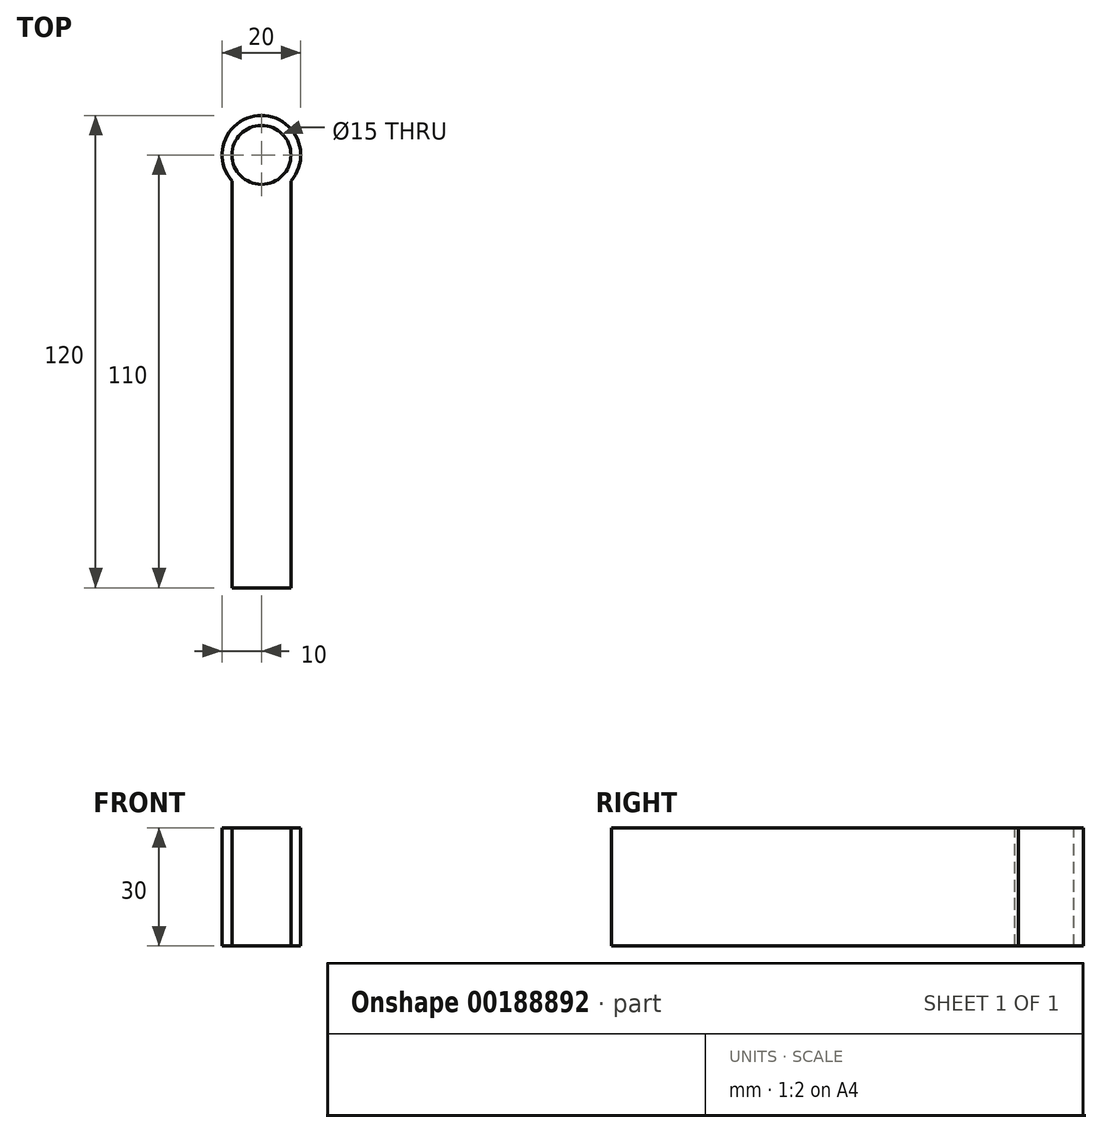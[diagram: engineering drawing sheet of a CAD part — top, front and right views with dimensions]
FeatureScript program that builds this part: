
annotation { "Feature Type Name" : "Feature", "Feature Type Description" : "" }
export const myFeature = defineFeature(function(context is Context, id is Id, definition is map)
    precondition{}
    {
        {
            var Q0;
            Q0=qCreatedBy(makeId("Top.planeOp"),FACE);
            var sketch = newSketch(context, id + "F0", { "sketchPlane" : qUnion([Q0])});
            skCircle(sketch, "E0", {"center": v(0, 0) * mm, "radius": 10 * mm});
            skSolve(sketch);
        }
        {
            var Q0;
            Q0=qSketchRegion(id+"F0",true);
            extrude(context, id + "F1", {"entities" : qUnion([Q0]), "depth" : 30 * mm});
        }
        {
            var Q0;
            Q0=qCreatedBy(makeId("Front.planeOp"),FACE);
            var sketch = newSketch(context, id + "F2", { "sketchPlane" : qUnion([Q0])});
            skLineSegment(sketch, "E1.bottom", {"start": v(-7.5, 30) * mm, "end": v(7.5, 30) * mm});
            skLineSegment(sketch, "E1.top", {"start": v(-7.5, 0) * mm, "end": v(7.5, 0) * mm});
            skLineSegment(sketch, "E1.left", {"start": v(-7.5, 30) * mm, "end": v(-7.5, 0) * mm});
            skLineSegment(sketch, "E1.right", {"start": v(7.5, 30) * mm, "end": v(7.5, 0) * mm});
            skSolve(sketch);
        }
        {
            var Q0;
            Q0=qSketchRegion(id+"F2",true);
            extrude(context, id + "F3", {"entities" : qUnion([Q0]), "operationType" : NewBodyOperationType.ADD, "depth" : 110 * mm});
        }
        {
            var Q0;
            Q0=makeQuery(id+"F3.boolean.opBoolean","MERGE",FACE,{"derivedFrom":[makeQuery(id+"F1.opExtrude","CAP_FACE",FACE,{"disambiguationData":[OSD([sQuery(id+"F0.wireOp",EDGE,"E0")])],"isStart":false}),makeQuery(id+"F3.opExtrude","SWEPT_FACE",FACE,{"disambiguationData":[OSD([sQuery(id+"F2.wireOp",EDGE,"E1.bottom")])]})]});
            var sketch = newSketch(context, id + "F4", { "sketchPlane" : qUnion([Q0])});
            skCircle(sketch, "E2", {"center": v(0, 0) * mm, "radius": 7.5 * mm});
            skSolve(sketch);
        }
        {
            var Q0;
            Q0=qSketchRegion(id+"F4",true);
            extrude(context, id + "F5", {"entities" : qUnion([Q0]), "operationType" : NewBodyOperationType.REMOVE, "endBound" : BoundingType.UP_TO_NEXT, "oppositeDirection" : true, "depth" : 25 * mm});
        }
    });
